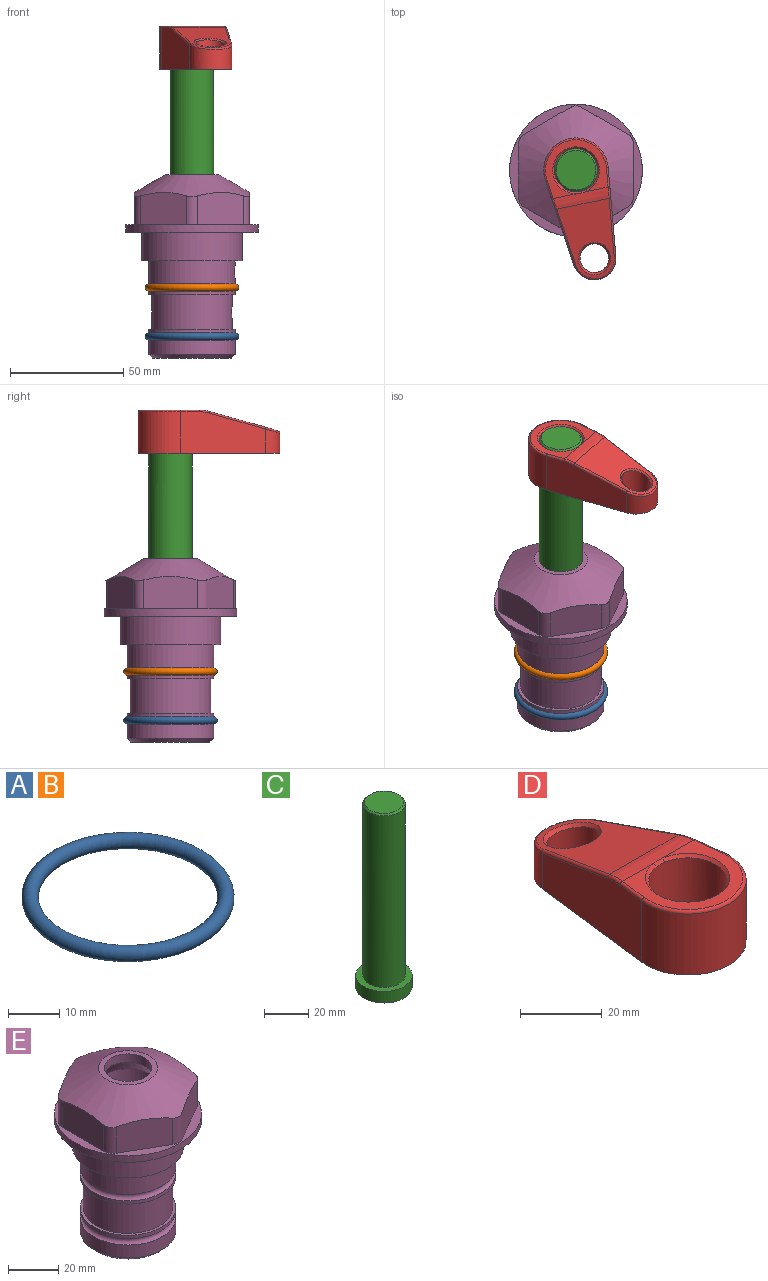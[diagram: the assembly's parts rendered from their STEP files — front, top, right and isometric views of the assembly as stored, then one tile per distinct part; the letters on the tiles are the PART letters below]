
ASSEMBLY  parts=5 mates=4
PART A: 1 faces, bbox 44.7x44.7x3.2 mm
  f0: torus R=19.05mm, axis (0,0,1), area 1193.9mm2
PART B: same geometry as A
PART C: 6 faces, bbox 25.4x25.4x101.6 mm
  f0: plane 17.46x17.46mm, normal (0,0,1), area 239.5mm2, adj f5
  f1: plane 25.4x25.4mm, normal (0,0,-1), area 506.7mm2, adj f2
  f2: cylinder r=12.7mm len=25.4mm, axis (0,0,1), area 506.7mm2, adj f1,f3
  f3: plane 25.4x25.4mm, normal (0,0,1), area 221.7mm2, adj f2,f4
  f4: cylinder r=9.53mm len=94.46mm, axis (0,0,1), area 5653mm2, adj f3,f5
  f5: cone r=8.73mm half-angle=45deg, axis (0,0,-1), area 64.4mm2, adj f0,f4
PART D: 31 faces, bbox 31.7x65.5x19.8 mm
  f0: plane 39.12x18.26mm, normal (0.99,0.12,0), area 612.2mm2, adj f1,f4,f7,f11,f13,f15
  f1: cylinder r=9.53mm len=18.91mm, axis (0,0,-1), area 296.1mm2, adj f0,f2,f7,f17
  f2: plane 39.12x18.26mm, normal (-0.99,0.12,0), area 612.2mm2, adj f1,f4,f7,f12,f14,f16
  f3: cylinder r=6.35mm len=12.7mm, axis (0,0,-1), area 362.4mm2, adj f7,f18
  f4: cylinder r=14.29mm len=28.58mm, axis (0,0,-1), area 882.2mm2, adj f0,f2,f7,f10
  f5: cylinder r=9.53mm len=19.05mm, axis (0,0,-1), area 1092.6mm2, adj f7,f19,f20
  f6: plane 26.99x23.69mm, normal (0,0,1), area 216.2mm2, adj f9,f10,f11,f12,f19
  f7: plane 63.5x28.58mm, normal (0,0,-1), area 661.8mm2, adj f0,f1,f2,f3,f4,f5,f22,f23
  f8: plane 33.52x23.6mm, normal (0,0.26,0.97), area 486mm2, adj f9,f15,f16,f17,f18
  f9: cylinder r=19.05mm len=24.72mm, axis (1,0,0), area 120.4mm2, adj f6,f8,f13,f14,f20
  f10: torus R=13.49mm, axis (0,0,1), area 59mm2, adj f4,f6,f11,f12
  f11: cylinder r=0.79mm len=8.67mm, axis (0.12,-0.99,0), area 10.8mm2, adj f0,f6,f10,f13
  f12: cylinder r=0.79mm len=8.67mm, axis (0.12,0.99,0), area 10.8mm2, adj f2,f6,f10,f14
  f13: bspline ~4.95x1.42mm, area 6.1mm2, adj f0,f9,f11,f15
  f14: bspline ~4.95x1.42mm, area 6.1mm2, adj f2,f9,f12,f16
  f15: cylinder r=0.79mm len=25.95mm, axis (0.12,-0.96,0.26), area 32.9mm2, adj f0,f8,f13,f17
  f16: cylinder r=0.79mm len=25.95mm, axis (0.12,0.96,-0.26), area 32.9mm2, adj f2,f8,f14,f17
  f17: bspline ~18.91x8.38mm, area 30mm2, adj f1,f8,f15,f16
  f18: bspline ~14.29x14.29mm, area 48.3mm2, adj f3,f8
  f19: cone r=9.53mm half-angle=45deg, axis (0,0,1), area 66.5mm2, adj f5,f6,f20
  f20: bspline ~3.22x0.96mm, area 3.5mm2, adj f5,f9,f19
  f21: plane 2.75x2.72mm, normal (0,0,-1), area 2.9mm2, adj f23,f25,f28
  f22: plane 23.05x15.88mm, normal (-0.99,-0.12,0), area 323.6mm2, adj f7,f25,f26,f27,f28,f29
  f23: plane 23.05x15.88mm, normal (0.99,-0.12,0), area 323.6mm2, adj f7,f21,f25,f27,f28,f30
  f24: cylinder r=9.53mm len=10.69mm, axis (0,0,-1), area 114.7mm2, adj f7,f27,f29,f30
  f25: cylinder r=12.7mm len=20.59mm, axis (0,0,-1), area 381.1mm2, adj f7,f21,f22,f23,f26,f28
  f26: plane 2.75x2.72mm, normal (0,0,-1), area 2.9mm2, adj f22,f25,f28
  f27: plane 19.72x18.37mm, normal (0,-0.26,-0.97), area 291.8mm2, adj f22,f23,f24,f28,f29,f30
  f28: cylinder r=15.88mm len=19.92mm, axis (1,0,0), area 54.8mm2, adj f21,f22,f23,f25,f26,f27
  f29: cylinder r=1.59mm len=11mm, axis (0,0,-1), area 34.7mm2, adj f7,f22,f24,f27
  f30: cylinder r=1.59mm len=11mm, axis (0,0,-1), area 34.7mm2, adj f7,f23,f24,f27
PART E: 36 faces, bbox 58.7x58.7x81 mm
  f0: cylinder r=17.78mm len=35.56mm, axis (0,0,1), area 1670.8mm2, adj f23,f24,f31
  f1: cylinder r=19.05mm len=38.1mm, axis (0,0,1), area 1191.9mm2, adj f26,f27,f30
  f2: plane 58.66x58.66mm, normal (0,0,-1), area 1150.6mm2, adj f3,f28
  f3: cylinder r=29.33mm len=58.66mm, axis (0,0,-1), area 585.1mm2, adj f2,f4
  f4: plane 58.66x58.66mm, normal (0,0,1), area 475.9mm2, adj f3,f5,f6,f7,f8,f9,f10,f11
  f5: plane 20.32x14.34mm, normal (-0.5,0.87,0), area 324.4mm2, adj f4,f15,f16,f17
  f6: plane 20.32x14.34mm, normal (0.5,0.87,0), area 324.4mm2, adj f4,f14,f15,f17
  f7: plane 23.48x14.34mm, normal (1,0,0), area 324.4mm2, adj f4,f13,f14,f17
  f8: plane 20.32x14.34mm, normal (0.5,-0.87,0), area 324.4mm2, adj f4,f12,f13,f17
  f9: plane 20.32x14.34mm, normal (-0.5,-0.87,0), area 324.4mm2, adj f4,f11,f12,f17
  f10: plane 23.48x14.34mm, normal (-1,0,0), area 324.4mm2, adj f4,f11,f16,f17
  f11: cylinder r=5.08mm len=12.85mm, axis (0,0,-1), area 67.2mm2, adj f4,f9,f10,f17
  f12: cylinder r=5.08mm len=12.85mm, axis (0,0,-1), area 67.2mm2, adj f4,f8,f9,f17
  f13: cylinder r=5.08mm len=12.85mm, axis (0,0,-1), area 67.2mm2, adj f4,f7,f8,f17
  f14: cylinder r=5.08mm len=12.85mm, axis (0,0,-1), area 67.2mm2, adj f4,f6,f7,f17
  f15: cylinder r=5.08mm len=12.85mm, axis (0,0,-1), area 67.2mm2, adj f4,f5,f6,f17
  f16: cylinder r=5.08mm len=12.85mm, axis (0,0,-1), area 67.2mm2, adj f4,f5,f10,f17
  f17: cone r=11.73mm half-angle=60deg, axis (0,0,-1), area 2071.8mm2, adj f5,f6,f7,f8,f9,f10,f11,f12
  f18: plane 23.46x23.46mm, normal (0,0,1), area 147.4mm2, adj f17,f35
  f19: plane 34.93x34.93mm, normal (0,0,-1), area 958mm2, adj f29
  f20: cylinder r=19.05mm len=38.1mm, axis (0,0,1), area 760.1mm2, adj f21,f29
  f21: torus R=19.05mm, axis (0,0,1), area 565.3mm2, adj f20,f22
  f22: cylinder r=19.05mm len=38.1mm, axis (0,0,1), area 190mm2, adj f21,f23
  f23: plane 38.1x38.1mm, normal (0,0,1), area 146.9mm2, adj f0,f22
  f24: plane 38.1x38.1mm, normal (0,0,-1), area 146.9mm2, adj f0,f25
  f25: cylinder r=19.05mm len=38.1mm, axis (0,0,1), area 190mm2, adj f24,f26
  f26: torus R=19.05mm, axis (0,0,1), area 565.3mm2, adj f1,f25
  f27: plane 44.45x44.45mm, normal (0,0,-1), area 411.7mm2, adj f1,f28
  f28: cylinder r=22.23mm len=44.45mm, axis (0,0,1), area 1773.5mm2, adj f2,f27
  f29: cone r=19.05mm half-angle=45deg, axis (0,0,1), area 257.5mm2, adj f19,f20
  f30: cylinder r=3.17mm len=6.75mm, axis (-1,0,0), area 128mm2, adj f1,f33
  f31: cylinder r=3.17mm len=6.35mm, axis (-1,0,0), area 102.5mm2, adj f0,f33
  f32: plane 25.4x25.4mm, normal (0,0,1), area 506.7mm2, adj f33
  f33: cylinder r=12.7mm len=66.42mm, axis (0,0,-1), area 5236.2mm2, adj f30,f31,f32,f34
  f34: cone r=9.53mm half-angle=30deg, axis (0,0,-1), area 443.4mm2, adj f33,f35
  f35: cylinder r=9.53mm len=19.05mm, axis (0,0,-1), area 240.9mm2, adj f18,f34
PLACE A t=(0,0,-21.59)mm
PLACE B at identity
PLACE C rot(axis=(0,0,-1),168.2deg) t=(0,0,27.55)mm
PLACE D rot(axis=(0,0,-1),168.2deg) t=(0,0,27.55)mm
PLACE E at identity fixed
MATE cylindrical C.f2 <-> E.f0  axis (0,0,-1) through (0,0,-10.55)mm
MATE fastened A.f0 <-> E.f0  axis (0,0,1) through (0,0,-46.1)mm
MATE fastened D.f4 <-> C.f2  axis (0,0,1) through (0,0,91.05)mm
MATE fastened B.f0 <-> E.f0  axis (0,0,1) through (0,0,-24.51)mm
